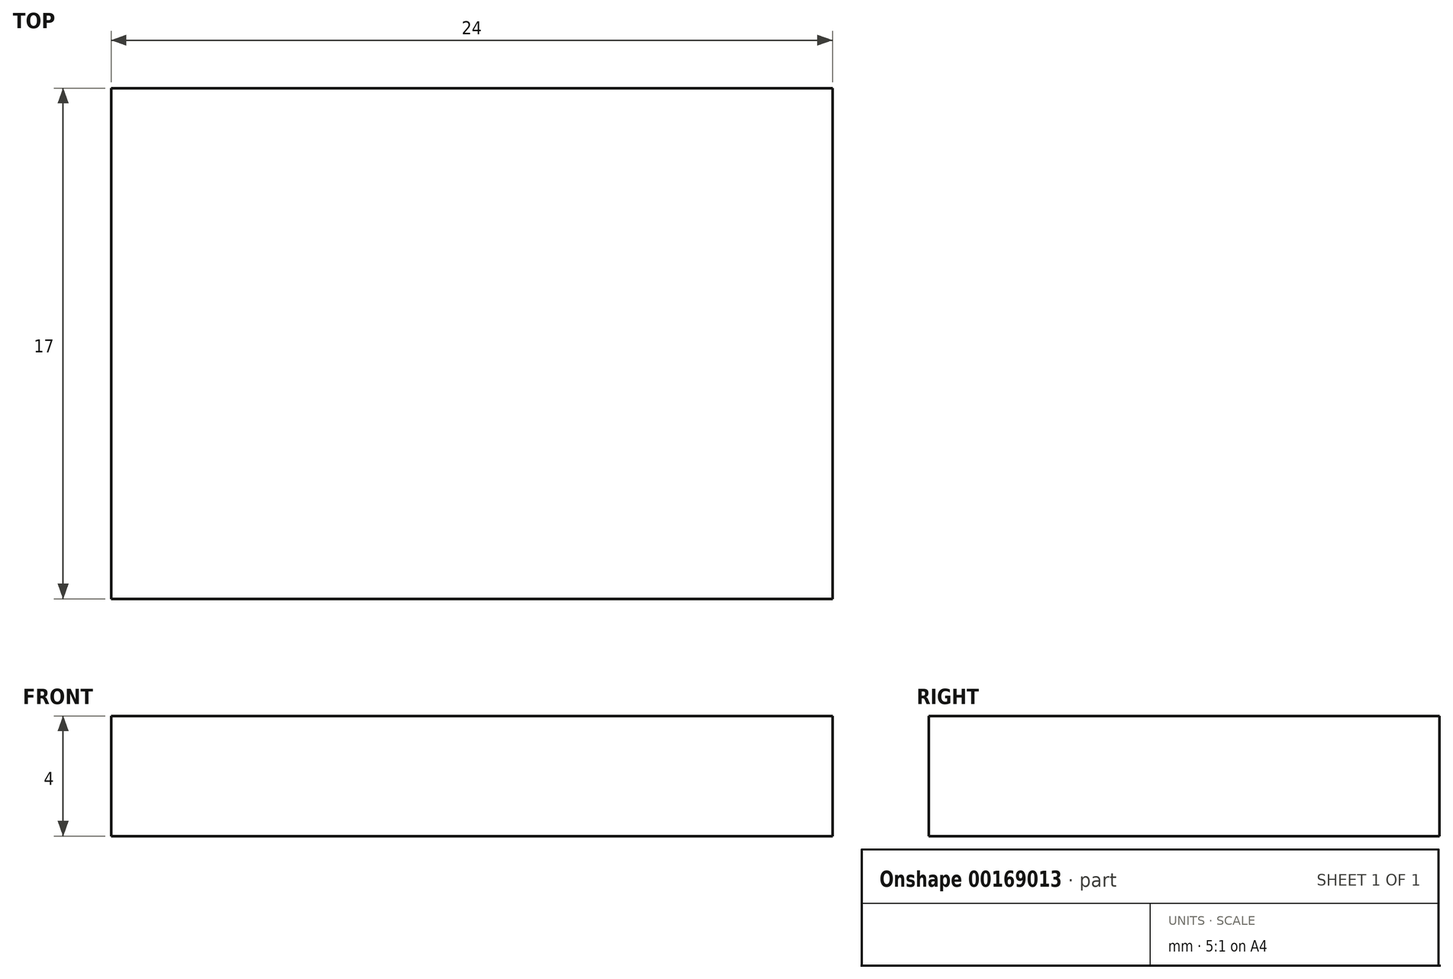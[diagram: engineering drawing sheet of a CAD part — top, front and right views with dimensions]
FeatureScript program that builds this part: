
annotation { "Feature Type Name" : "Feature", "Feature Type Description" : "" }
export const myFeature = defineFeature(function(context is Context, id is Id, definition is map)
    precondition{}
    {
        {
            var Q0;
            Q0=qCreatedBy(makeId("Top.planeOp"),FACE);
            var sketch = newSketch(context, id + "F0", { "sketchPlane" : qUnion([Q0])});
            skLineSegment(sketch, "E0.bottom", {"start": v(0, 17) * mm, "end": v(24, 17) * mm});
            skLineSegment(sketch, "E0.top", {"start": v(0, 0) * mm, "end": v(24, 0) * mm});
            skLineSegment(sketch, "E0.left", {"start": v(0, 17) * mm, "end": v(0, 0) * mm});
            skLineSegment(sketch, "E0.right", {"start": v(24, 17) * mm, "end": v(24, 0) * mm});
            skSolve(sketch);
        }
        {
            var Q0;
            Q0 = qSketchRegion(id + "F0", true);
            extrude(context, id + "F1", {"entities" : qUnion([Q0]), "depth" : 4 * mm});
        }
    });
